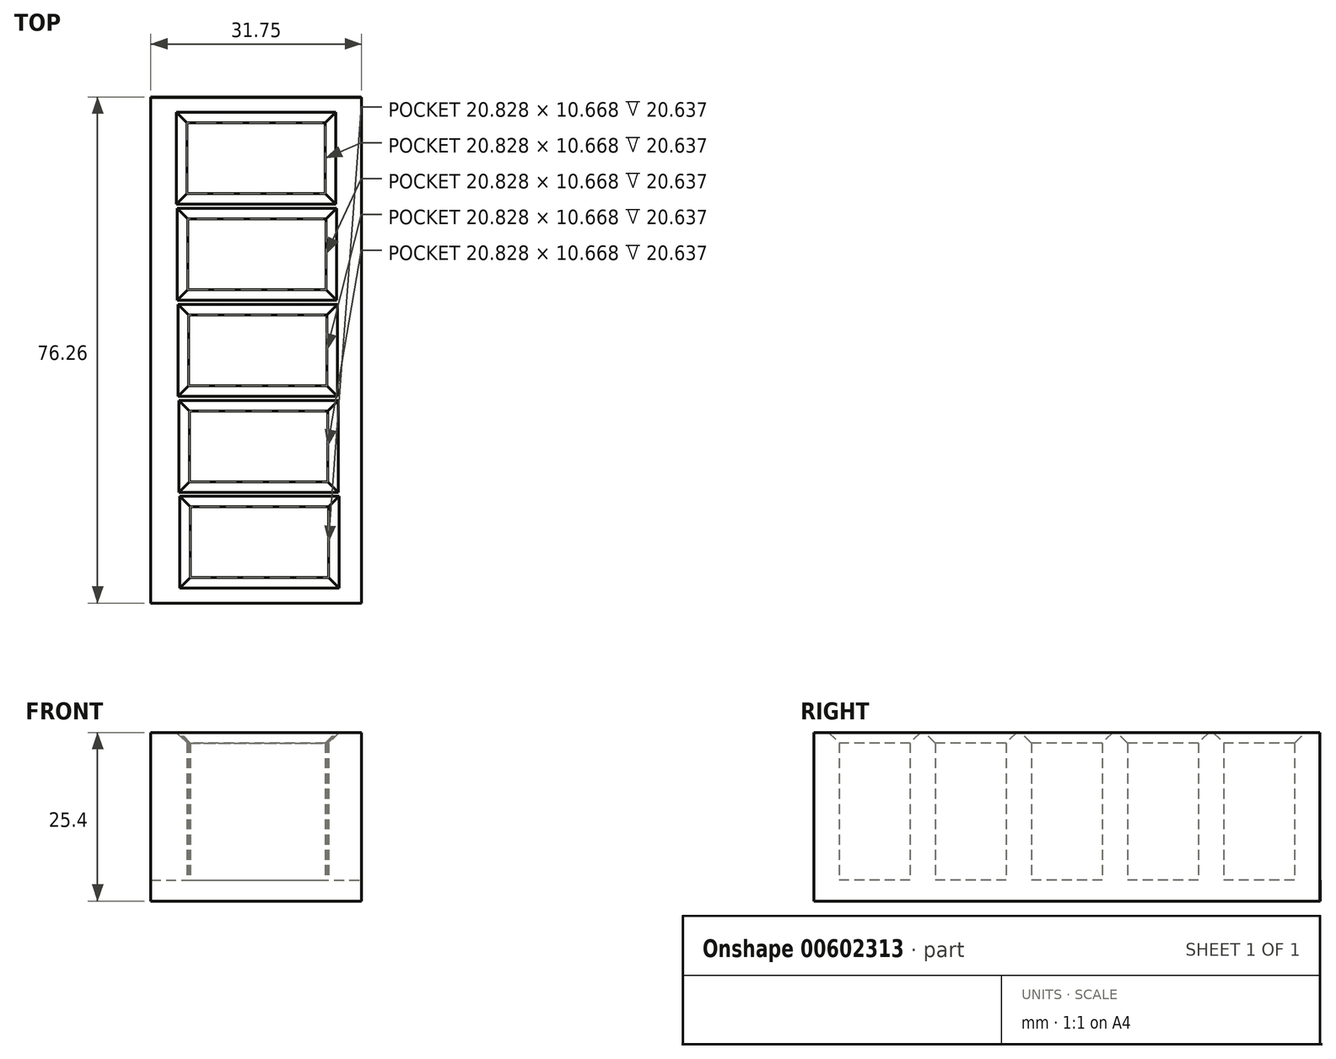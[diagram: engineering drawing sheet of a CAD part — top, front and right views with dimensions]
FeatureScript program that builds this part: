
annotation { "Feature Type Name" : "Feature", "Feature Type Description" : "" }
export const myFeature = defineFeature(function(context is Context, id is Id, definition is map)
    precondition{}
    {
        {
            var Q0;
            Q0=qCreatedBy(makeId("Top.planeOp"),FACE);
            var sketch = newSketch(context, id + "F0", { "sketchPlane" : qUnion([Q0])});
            skLineSegment(sketch, "E0.top", {"start": v(0, 76.2) * mm, "end": v(31.75, 76.2) * mm});
            skLineSegment(sketch, "E0.left", {"start": v(0, 0) * mm, "end": v(0, 76.2) * mm});
            skLineSegment(sketch, "E0.right", {"start": v(31.75, 0) * mm, "end": v(31.75, 76.2) * mm});
            skLineSegment(sketch, "E1.bottom", {"start": v(5.46, 72.4) * mm, "end": v(26.29, 72.4) * mm});
            skLineSegment(sketch, "E1.top", {"start": v(5.46, 61.72) * mm, "end": v(26.29, 61.72) * mm});
            skLineSegment(sketch, "E1.left", {"start": v(5.46, 72.4) * mm, "end": v(5.46, 61.72) * mm});
            skLineSegment(sketch, "E1.right", {"start": v(26.29, 72.4) * mm, "end": v(26.29, 61.72) * mm});
            skLineSegment(sketch, "E2", {"start": v(0, 0) * mm, "end": v(31.75, 0) * mm});
            skLineSegment(sketch, "E3.1.0.0", {"start": v(26.42, 57.91) * mm, "end": v(26.42, 47.24) * mm});
            skLineSegment(sketch, "E3.1.0.1", {"start": v(5.59, 57.91) * mm, "end": v(5.59, 47.24) * mm});
            skLineSegment(sketch, "E3.1.0.2", {"start": v(5.59, 47.24) * mm, "end": v(26.42, 47.24) * mm});
            skLineSegment(sketch, "E3.1.0.3", {"start": v(5.59, 57.91) * mm, "end": v(26.42, 57.91) * mm});
            skLineSegment(sketch, "E3.2.0.0", {"start": v(26.54, 43.44) * mm, "end": v(26.54, 32.77) * mm});
            skLineSegment(sketch, "E3.2.0.1", {"start": v(5.71, 43.44) * mm, "end": v(5.71, 32.77) * mm});
            skLineSegment(sketch, "E3.2.0.2", {"start": v(5.71, 32.77) * mm, "end": v(26.54, 32.77) * mm});
            skLineSegment(sketch, "E3.2.0.3", {"start": v(5.71, 43.44) * mm, "end": v(26.54, 43.44) * mm});
            skLineSegment(sketch, "E3.3.0.0", {"start": v(26.67, 28.96) * mm, "end": v(26.67, 18.29) * mm});
            skLineSegment(sketch, "E3.3.0.1", {"start": v(5.84, 28.96) * mm, "end": v(5.84, 18.29) * mm});
            skLineSegment(sketch, "E3.3.0.2", {"start": v(5.84, 18.29) * mm, "end": v(26.67, 18.29) * mm});
            skLineSegment(sketch, "E3.3.0.3", {"start": v(5.84, 28.96) * mm, "end": v(26.67, 28.96) * mm});
            skLineSegment(sketch, "E3.4.0.0", {"start": v(26.8, 14.48) * mm, "end": v(26.8, 3.81) * mm});
            skLineSegment(sketch, "E3.4.0.1", {"start": v(5.97, 14.48) * mm, "end": v(5.97, 3.81) * mm});
            skLineSegment(sketch, "E3.4.0.2", {"start": v(5.97, 3.81) * mm, "end": v(26.8, 3.81) * mm});
            skLineSegment(sketch, "E3.4.0.3", {"start": v(5.97, 14.48) * mm, "end": v(26.8, 14.48) * mm});
            skLineSegment(sketch, "E3.direction1", {"start": v(5.46, 61.72) * mm, "end": v(5.59, 47.24) * mm, "construction": true});
            skSolve(sketch);
        }
        {
            var Q0;
            Q0=makeQuery(id+"F0.imprint","IMPRINT",FACE,{"disambiguationData":[TD([[makeQuery(id+"F0.imprint","IMPRINT",EDGE,{"derivedFrom":sQuery(id+"F0.wireOp",EDGE,"E0.top")}),-1.0]])]});
            extrude(context, id + "F1", {"entities" : qUnion([Q0]), "depth" : 25.4 * mm, "offsetDistance" : 25.4 * mm});
        }
        {
            var Q0;
            Q0=qCreatedBy(makeId("Top.planeOp"),FACE);
            var sketch = newSketch(context, id + "F2", { "sketchPlane" : qUnion([Q0])});
            skLineSegment(sketch, "E4.bottom", {"start": v(31.7, 0) * mm, "end": v(0, 0) * mm});
            skLineSegment(sketch, "E4.top", {"start": v(31.7, 76.26) * mm, "end": v(0, 76.26) * mm});
            skLineSegment(sketch, "E4.left", {"start": v(31.7, 0) * mm, "end": v(31.7, 76.26) * mm});
            skLineSegment(sketch, "E4.right", {"start": v(0, 0) * mm, "end": v(0, 76.26) * mm});
            skSolve(sketch);
        }
        {
            var Q0;
            Q0=makeQuery(id+"F2.imprint","IMPRINT",FACE,{"disambiguationData":[TD([[makeQuery(id+"F2.imprint","IMPRINT",EDGE,{"derivedFrom":sQuery(id+"F2.wireOp",EDGE,"E4.bottom")}),-1.0]])]});
            extrude(context, id + "F3", {"entities" : qUnion([Q0]), "operationType" : NewBodyOperationType.ADD, "depth" : 3.17 * mm, "offsetDistance" : 25.4 * mm});
        }
        {
            var Q0;
            Q0=makeQuery(id+"F1.opExtrude","CAP_EDGE",EDGE,{"disambiguationData":[OSD([sQuery(id+"F0.wireOp",EDGE,"E3.4.0.1")])],"isStart":false});
            var Q1;
            Q1=makeQuery(id+"F1.opExtrude","CAP_EDGE",EDGE,{"disambiguationData":[OSD([sQuery(id+"F0.wireOp",EDGE,"E3.4.0.2")])],"isStart":false});
            var Q2;
            Q2=makeQuery(id+"F1.opExtrude","CAP_EDGE",EDGE,{"disambiguationData":[OSD([sQuery(id+"F0.wireOp",EDGE,"E3.4.0.0")])],"isStart":false});
            var Q3;
            Q3=makeQuery(id+"F1.opExtrude","CAP_EDGE",EDGE,{"disambiguationData":[OSD([sQuery(id+"F0.wireOp",EDGE,"E3.4.0.3")])],"isStart":false});
            var Q4;
            Q4=makeQuery(id+"F1.opExtrude","CAP_EDGE",EDGE,{"disambiguationData":[OSD([sQuery(id+"F0.wireOp",EDGE,"E3.3.0.2")])],"isStart":false});
            var Q5;
            Q5=makeQuery(id+"F1.opExtrude","CAP_EDGE",EDGE,{"disambiguationData":[OSD([sQuery(id+"F0.wireOp",EDGE,"E3.3.0.1")])],"isStart":false});
            var Q6;
            Q6=makeQuery(id+"F1.opExtrude","CAP_EDGE",EDGE,{"disambiguationData":[OSD([sQuery(id+"F0.wireOp",EDGE,"E3.3.0.0")])],"isStart":false});
            var Q7;
            Q7=makeQuery(id+"F1.opExtrude","CAP_EDGE",EDGE,{"disambiguationData":[OSD([sQuery(id+"F0.wireOp",EDGE,"E3.3.0.3")])],"isStart":false});
            var Q8;
            Q8=makeQuery(id+"F1.opExtrude","CAP_EDGE",EDGE,{"disambiguationData":[OSD([sQuery(id+"F0.wireOp",EDGE,"E3.2.0.2")])],"isStart":false});
            var Q9;
            Q9=makeQuery(id+"F1.opExtrude","CAP_EDGE",EDGE,{"disambiguationData":[OSD([sQuery(id+"F0.wireOp",EDGE,"E3.2.0.1")])],"isStart":false});
            var Q10;
            Q10=makeQuery(id+"F1.opExtrude","CAP_EDGE",EDGE,{"disambiguationData":[OSD([sQuery(id+"F0.wireOp",EDGE,"E3.2.0.0")])],"isStart":false});
            var Q11;
            Q11=makeQuery(id+"F1.opExtrude","CAP_EDGE",EDGE,{"disambiguationData":[OSD([sQuery(id+"F0.wireOp",EDGE,"E3.2.0.3")])],"isStart":false});
            var Q12;
            Q12=makeQuery(id+"F1.opExtrude","CAP_EDGE",EDGE,{"disambiguationData":[OSD([sQuery(id+"F0.wireOp",EDGE,"E3.1.0.3")])],"isStart":false});
            var Q13;
            Q13=makeQuery(id+"F1.opExtrude","CAP_EDGE",EDGE,{"disambiguationData":[OSD([sQuery(id+"F0.wireOp",EDGE,"E3.1.0.1")])],"isStart":false});
            var Q14;
            Q14=makeQuery(id+"F1.opExtrude","CAP_EDGE",EDGE,{"disambiguationData":[OSD([sQuery(id+"F0.wireOp",EDGE,"E3.1.0.2")])],"isStart":false});
            var Q15;
            Q15=makeQuery(id+"F1.opExtrude","CAP_EDGE",EDGE,{"disambiguationData":[OSD([sQuery(id+"F0.wireOp",EDGE,"E3.1.0.0")])],"isStart":false});
            var Q16;
            Q16=makeQuery(id+"F1.opExtrude","CAP_EDGE",EDGE,{"disambiguationData":[OSD([sQuery(id+"F0.wireOp",EDGE,"E1.top")])],"isStart":false});
            var Q17;
            Q17=makeQuery(id+"F1.opExtrude","CAP_EDGE",EDGE,{"disambiguationData":[OSD([sQuery(id+"F0.wireOp",EDGE,"E1.left")])],"isStart":false});
            var Q18;
            Q18=makeQuery(id+"F1.opExtrude","CAP_EDGE",EDGE,{"disambiguationData":[OSD([sQuery(id+"F0.wireOp",EDGE,"E1.bottom")])],"isStart":false});
            var Q19;
            Q19=makeQuery(id+"F1.opExtrude","CAP_EDGE",EDGE,{"disambiguationData":[OSD([sQuery(id+"F0.wireOp",EDGE,"E1.right")])],"isStart":false});
            chamfer(context, id + "F4", {"entities" : qUnion([Q0, Q1, Q2, Q3, Q4, Q5, Q6, Q7, Q8, Q9, Q10, Q11, Q12, Q13, Q14, Q15, Q16, Q17, Q18, Q19]), "width" : 1.59 * mm, "tangentPropagation" : true});
        }
    });
